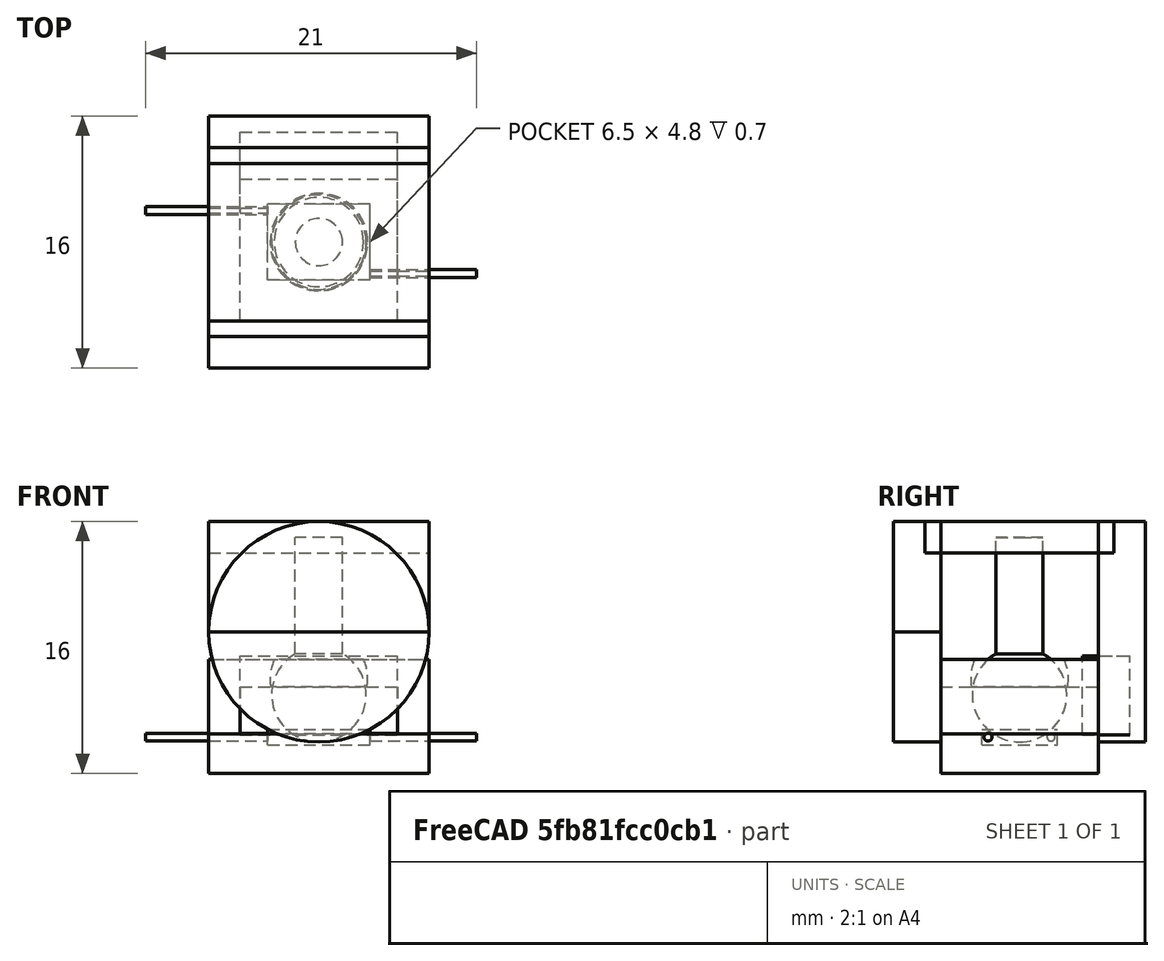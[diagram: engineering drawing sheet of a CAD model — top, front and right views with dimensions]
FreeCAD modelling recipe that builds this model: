
FCSTD DOCUMENT  (FreeCAD 0.16R6710 (Git))
Label: Feet sensors0.5
License: All rights reserved
LicenseURL: http://en.wikipedia.org/wiki/All_rights_reserved
objects: Part::Box×10, Part::Cylinder×8, Part::Fuse×7, Part::Cut×5, Part::Sphere×2, Part::MultiCommon×1
note: 33 computed .brp shape members not serialized (recipe doc carries the construction recipe); baked Part::Feature solids carry a one-line shape summary decoded from their .brp

FEATURE [Part::Sphere] Sphere
  Angle1 = -90
  Angle2 = 90
  Angle3 = 360
  Radius = 3
FEATURE [Part::Cylinder] Cylinder
  Angle = 360
  Height = 10
  Radius = 1.5
FEATURE [Part::Box] Box  label="Cube"
  Height = 1
  Length = 6.5
  Placement = pos=(-3.25,-2.4,-4.2) rot=(0,0,1;0rad)
  Width = 4.8
FEATURE [Part::Cylinder] Cylinder001
  Angle = 360
  Height = 10
  Placement = pos=(-11,2,-3.7) rot=(0,1,0;1.5708rad)
  Radius = 0.25
FEATURE [Part::Cylinder] Cylinder002
  Angle = 360
  Height = 10
  Placement = pos=(0,-2,-3.7) rot=(0,1,0;1.5708rad)
  Radius = 0.25
FEATURE [Part::Box] Box001  label="Cube001"
  Height = 7.25
  Length = 14
  Placement = pos=(-7,-5,-6) rot=(0,0,1;0rad)
  Width = 10
FEATURE [Part::Box] Box002  label="Cube002"
  Height = 1
  Length = 6.5
  Placement = pos=(-3.25,-2.4,-4.2) rot=(0,0,1;0rad)
  Width = 4.8
FEATURE [Part::Cylinder] Cylinder003
  Angle = 360
  Height = 10
  Placement = pos=(-11,2,-3.7) rot=(0,1,0;1.5708rad)
  Radius = 0.25
FEATURE [Part::Cylinder] Cylinder004
  Angle = 360
  Height = 10
  Placement = pos=(0,-2,-3.7) rot=(0,1,0;1.5708rad)
  Radius = 0.25
FEATURE [Part::Fuse] Fusion
  Base = -> Cylinder003
  Tool = -> Cylinder004
FEATURE [Part::Fuse] Fusion001
  Base = -> Box002
  Tool = -> Fusion
FEATURE [Part::Box] Box003  label="Cube003"
  Height = 3
  Length = 10
  Placement = pos=(-5,-6,-3.5) rot=(0,0,1;0rad)
  Width = 12
FEATURE [Part::Cut] Cut
  Base = -> Box001
  Tool = -> Box003
FEATURE [Part::Cut] Cut001
  Base = -> Cut
  Tool = -> Fusion001
FEATURE [Part::Fuse] Fusion002
  Base = -> Cylinder001
  Tool = -> Cylinder002
FEATURE [Part::Fuse] Fusion003  label="Switch"
  Base = -> Box
  Tool = -> Fusion002
FEATURE [Part::Box] Box004  label="Cube004"
  Height = 5
  Length = 10
  Placement = pos=(-5,4,-3.55) rot=(0,0,1;0rad)
  Width = 3
FEATURE [Part::Sphere] Sphere001
  Angle1 = -90
  Angle2 = 90
  Angle3 = 360
  Radius = 3.1
FEATURE [Part::Cylinder] Cylinder005
  Angle = 360
  Height = 10
  Placement = pos=(0,0,0.5) rot=(0,0,1;0rad)
  Radius = 2.5
FEATURE [Part::Fuse] Fusion004
  Base = -> Sphere001
  Tool = -> Cylinder005
FEATURE [Part::Cut] Cut002
  Base = -> Cut001
  Tool = -> Fusion004
FEATURE [Part::Fuse] Fusion005  label="Ball and Screw"
  Base = -> Sphere
  Placement = pos=(0,0,-1) rot=(0,0,1;0rad)
  Tool = -> Cylinder
FEATURE [Part::Cut] Cut003
  Base = -> Cut001
  Tool = -> Fusion004
FEATURE [Part::Box] Box005  label="Cube005"
  Height = 8
  Length = 21
  Placement = pos=(-9,-7,-3.5) rot=(0,0,1;0rad)
  Width = 17
FEATURE [Part::Box] Box006  label="Cube006"
  Height = 12
  Length = 21
  Placement = pos=(-9,-7,-3.5) rot=(0,0,1;0rad)
  Width = 17
FEATURE [Part::Cut] Cut004  label="Bottom Switch holder"
  Base = -> Cut003
  Tool = -> Box005
FEATURE [Part::MultiCommon] Common  label="Ball and screw holder"
  Shapes = -> [Cut002,Box006]
FEATURE [Part::Box] Box007  label="Cube007"
  Height = 7
  Length = 14
  Placement = pos=(-7,5,3) rot=(0,0,1;0rad)
  Width = 3
FEATURE [Part::Cylinder] Cylinder006
  Angle = 360
  Height = 3
  Placement = pos=(0,8,3) rot=(1,0,0;1.5708rad)
  Radius = 7
FEATURE [Part::Fuse] Fusion006
  Base = -> Box007
  Tool = -> Cylinder006
FEATURE [Part::Box] Box008  label="Cube008"
  Height = 7
  Length = 14
  Placement = pos=(-7,-8,3) rot=(0,0,1;0rad)
  Width = 3
FEATURE [Part::Cylinder] Cylinder007
  Angle = 360
  Height = 3
  Placement = pos=(0,-5,3) rot=(1,0,0;1.5708rad)
  Radius = 7
FEATURE [Part::Box] Box009  label="Cube009"
  Height = 2
  Length = 14
  Placement = pos=(-7,-6,8) rot=(0,0,1;0rad)
  Width = 12
